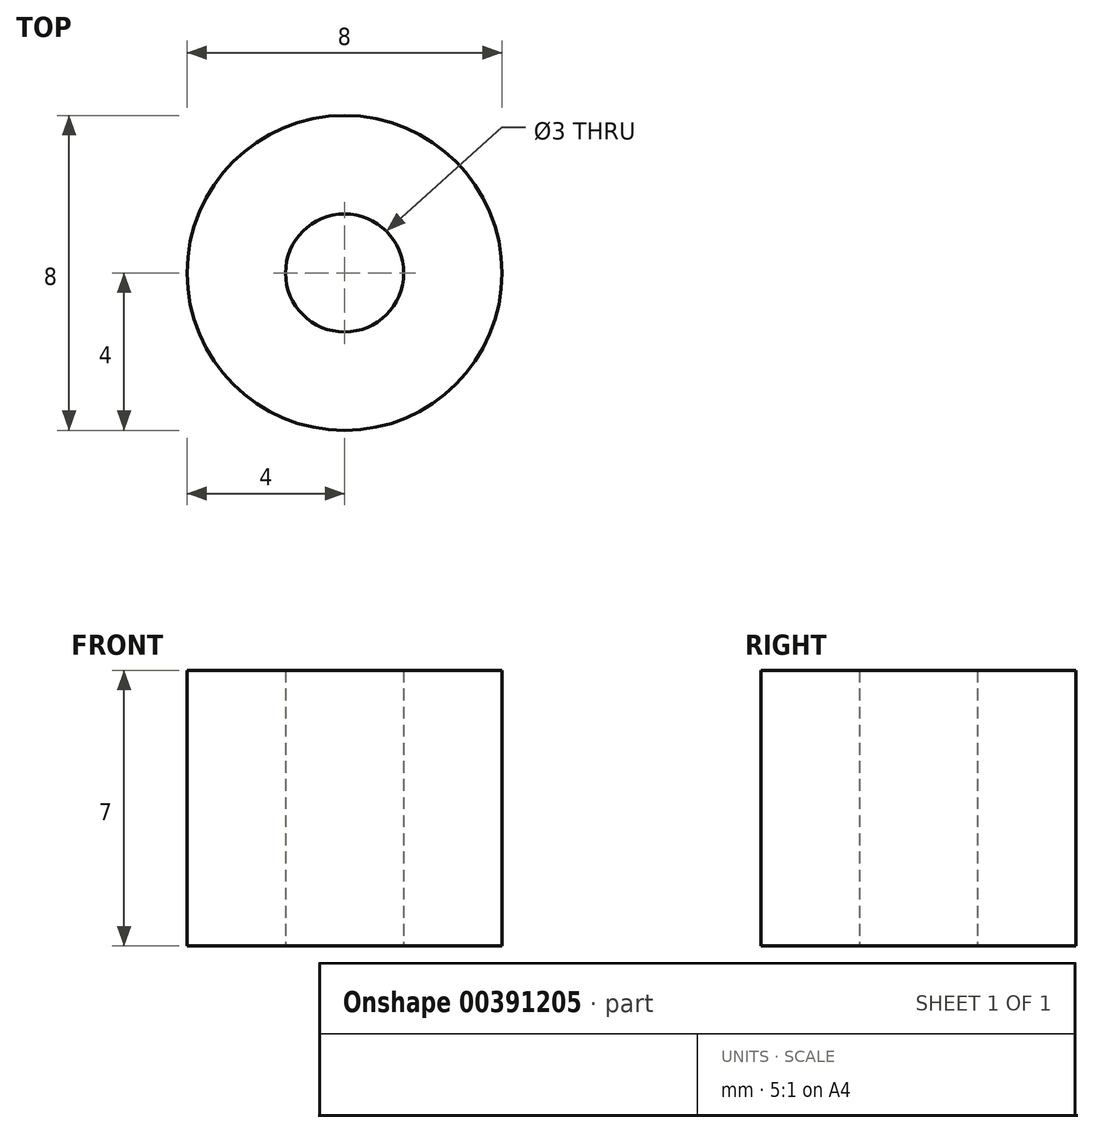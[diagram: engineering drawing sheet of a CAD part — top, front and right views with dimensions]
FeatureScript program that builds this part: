
annotation { "Feature Type Name" : "Feature", "Feature Type Description" : "" }
export const myFeature = defineFeature(function(context is Context, id is Id, definition is map)
    precondition{}
    {
        {
            var Q0;
            Q0=qCreatedBy(makeId("Top.planeOp"),FACE);
            var sketch = newSketch(context, id + "F0", { "sketchPlane" : qUnion([Q0])});
            skCircle(sketch, "E0", {"center": v(0, 0) * mm, "radius": 4 * mm});
            skCircle(sketch, "E1", {"center": v(0, 0) * mm, "radius": 1.5 * mm});
            skSolve(sketch);
        }
        {
            var Q0;
            Q0=makeQuery(id+"F0.imprint","IMPRINT",FACE,{"disambiguationData":[TD([[makeQuery(id+"F0.imprint","IMPRINT",EDGE,{"derivedFrom":sQuery(id+"F0.wireOp",EDGE,"E0")}),1.0]])]});
            extrude(context, id + "F1", {"entities" : qUnion([Q0]), "depth" : 7 * mm});
        }
    });
